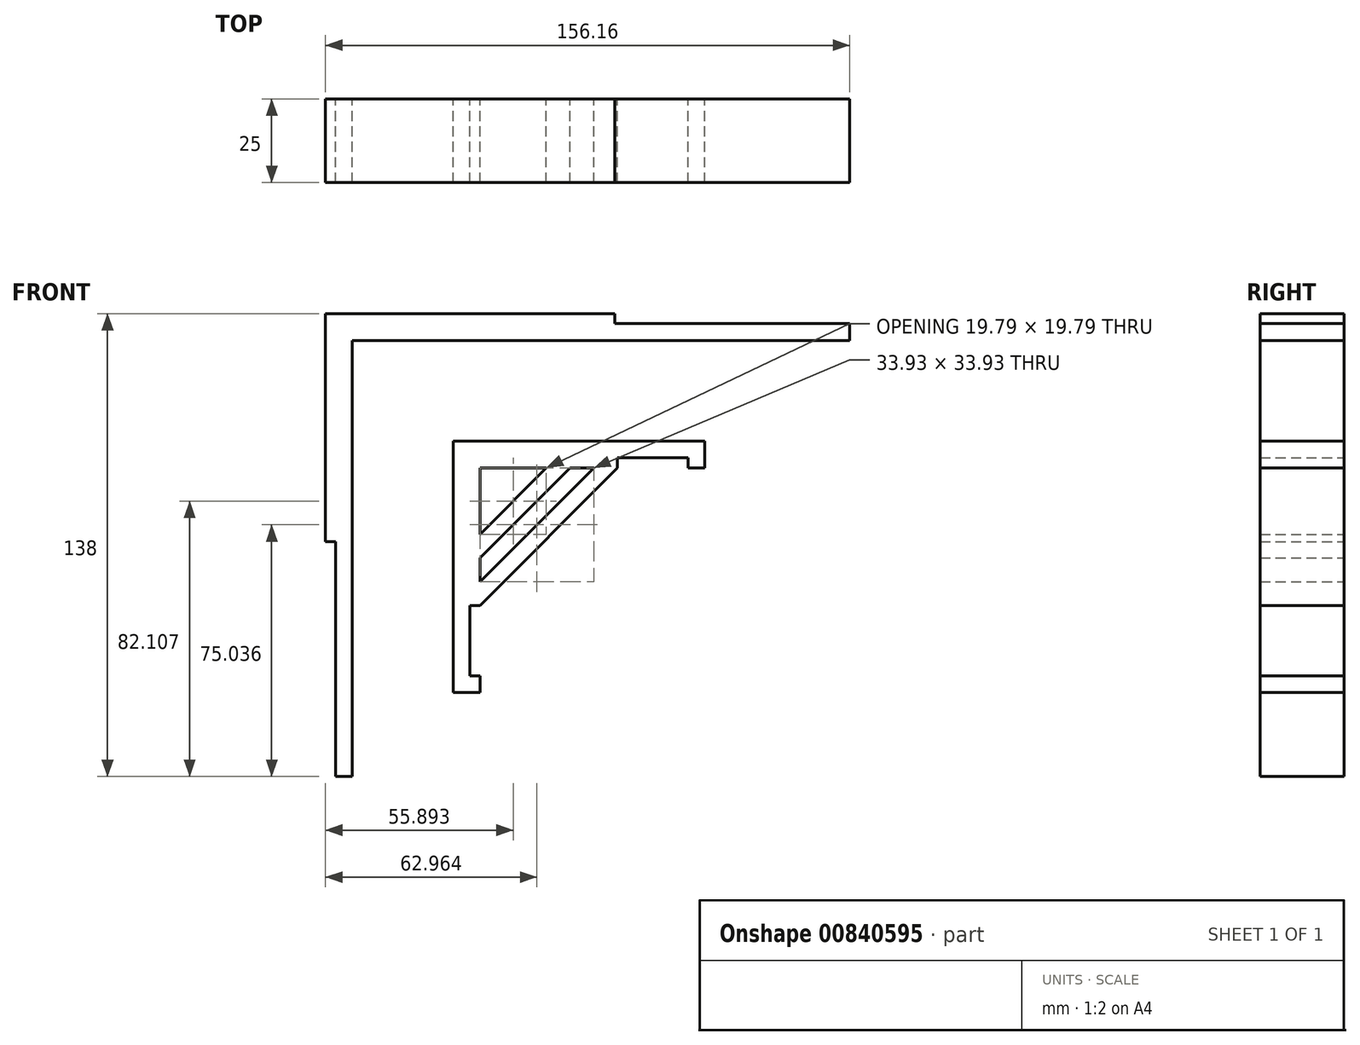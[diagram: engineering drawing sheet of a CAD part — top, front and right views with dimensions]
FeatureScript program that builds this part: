
annotation { "Feature Type Name" : "Feature", "Feature Type Description" : "" }
export const myFeature = defineFeature(function(context is Context, id is Id, definition is map)
    precondition{}
    {
        {
            var Q0;
            Q0=qCreatedBy(makeId("Front.planeOp"),FACE);
            var sketch = newSketch(context, id + "F0", { "sketchPlane" : qUnion([Q0])});
            skLineSegment(sketch, "E0", {"start": v(0, 0) * mm, "end": v(0, -75) * mm});
            skLineSegment(sketch, "E1", {"start": v(0, -75) * mm, "end": v(5, -75) * mm});
            skLineSegment(sketch, "E2", {"start": v(5, -75) * mm, "end": v(8, -75) * mm});
            skLineSegment(sketch, "E3", {"start": v(8, -75) * mm, "end": v(8, -70) * mm});
            skLineSegment(sketch, "E4", {"start": v(8, -70) * mm, "end": v(5, -70) * mm});
            skLineSegment(sketch, "E5", {"start": v(5, -70) * mm, "end": v(5, -49) * mm});
            skLineSegment(sketch, "E6", {"start": v(5, -49) * mm, "end": v(8, -49) * mm});
            skLineSegment(sketch, "E7", {"start": v(8, -49) * mm, "end": v(8, 0) * mm});
            skLineSegment(sketch, "E8", {"start": v(8, 0) * mm, "end": v(0, 0) * mm});
            skLineSegment(sketch, "E9", {"start": v(0, 0) * mm, "end": v(75, 0) * mm});
            skLineSegment(sketch, "E10", {"start": v(75, 0) * mm, "end": v(75, -8) * mm});
            skLineSegment(sketch, "E11", {"start": v(75, -8) * mm, "end": v(70, -8) * mm});
            skLineSegment(sketch, "E12", {"start": v(70, -8) * mm, "end": v(70, -5) * mm});
            skLineSegment(sketch, "E13", {"start": v(70, -5) * mm, "end": v(49, -5) * mm});
            skLineSegment(sketch, "E14", {"start": v(49, -5) * mm, "end": v(49, -8) * mm});
            skLineSegment(sketch, "E15", {"start": v(49, -8) * mm, "end": v(0, -8) * mm});
            skLineSegment(sketch, "E16", {"start": v(49, -8) * mm, "end": v(8, -49) * mm});
            skLineSegment(sketch, "E17.0", {"start": v(45.46, -4.46) * mm, "end": v(4.46, -45.46) * mm});
            skLineSegment(sketch, "E18.0", {"start": v(41.93, -0.93) * mm, "end": v(0.93, -41.93) * mm});
            skLineSegment(sketch, "E19.0", {"start": v(38.4, 2.6) * mm, "end": v(-2.6, -38.4) * mm});
            skSolve(sketch);
        }
        {
            var Q0;
            Q0 = qSketchRegion(id + "F0", true);
            var Q1;
            {var subQ0=sQuery(id+"F0.wireOp",EDGE,"E18.0");var subQ1=sQuery(id+"F0.wireOp",EDGE,"E7");var subQ2=makeQuery(id+"F0.imprint","INTERSECT",VERTEX,{"derivedFrom":[subQ1,subQ0]});Q1=makeQuery(id+"F0.imprint","IMPRINT",FACE,{"disambiguationData":[TD([[makeQuery(id+"F0.imprint","IMPRINT",EDGE,{"disambiguationData":[TD([[subQ2,-1.0]])],"derivedFrom":subQ1}),-1.0]])]});}
            extrude(context, id + "F1", {"entities" : qUnion([Q0, Q1]), "depth" : 25 * mm, "offsetDistance" : 25 * mm});
        }
        {
            var Q0;
            Q0=qCreatedBy(makeId("Front.planeOp"),FACE);
            var sketch = newSketch(context, id + "F2", { "sketchPlane" : qUnion([Q0])});
            skLineSegment(sketch, "E20", {"start": v(0, 0) * mm, "end": v(-30, 0) * mm, "construction": true});
            skLineSegment(sketch, "E21", {"start": v(0, 0) * mm, "end": v(0, 30) * mm, "construction": true});
            skLineSegment(sketch, "E22", {"start": v(0, 30) * mm, "end": v(118.16, 30) * mm, "construction": true});
            skLineSegment(sketch, "E23", {"start": v(-30, 0) * mm, "end": v(-30, -77.26) * mm, "construction": true});
            skLineSegment(sketch, "E24", {"start": v(-30, 0) * mm, "end": v(-30, 30) * mm, "construction": true});
            skLineSegment(sketch, "E25", {"start": v(-30, 30) * mm, "end": v(0, 30) * mm, "construction": true});
            skLineSegment(sketch, "E26", {"start": v(-30, 30) * mm, "end": v(-30, -100) * mm});
            skLineSegment(sketch, "E27", {"start": v(-30, -100) * mm, "end": v(-35, -100) * mm});
            skLineSegment(sketch, "E28", {"start": v(-35, -100) * mm, "end": v(-35, -30) * mm});
            skLineSegment(sketch, "E29", {"start": v(-35, -30) * mm, "end": v(-38, -30) * mm});
            skLineSegment(sketch, "E30", {"start": v(-38, -30) * mm, "end": v(-38, 60.87) * mm});
            skLineSegment(sketch, "E31", {"start": v(118.16, 30) * mm, "end": v(118.16, 35) * mm});
            skLineSegment(sketch, "E32", {"start": v(-30, 30) * mm, "end": v(118.16, 30) * mm});
            skLineSegment(sketch, "E33", {"start": v(118.16, 35) * mm, "end": v(48.16, 35) * mm});
            skLineSegment(sketch, "E34", {"start": v(48.16, 35) * mm, "end": v(48.16, 38) * mm});
            skLineSegment(sketch, "E35", {"start": v(48.16, 38) * mm, "end": v(-38, 38) * mm});
            skSolve(sketch);
        }
        {
            var Q0;
            Q0 = qSketchRegion(id + "F2", true);
            extrude(context, id + "F3", {"entities" : qUnion([Q0]), "depth" : 25 * mm, "offsetDistance" : 25 * mm});
        }
    });
